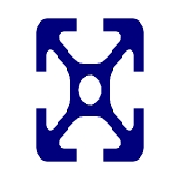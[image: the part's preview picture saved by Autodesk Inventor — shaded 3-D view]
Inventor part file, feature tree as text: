
AUTODESK INVENTOR PART (.ipt)
format: ipt  version: 2020 (Build 240168000, 168)  size: 276,480 bytes
history: native  units: mm
features: other x16, sketch x8, plane x1, split x1
ambient origin geometry x8: Origin, YZ Plane, XZ Plane, XY Plane, X Axis, Y Axis, Z Axis, Center Point
bodies: Body (feature_tree)
feature tree (26):
  other  "Řízená délka"
  other  "Těleso1"
  other  "Start Plane"
  other  "End Plane"
  other  "iFeatureSketch"
  other  "DRAZKA_20:1"
  other  "DRAZKA_20:2"
  other  "DRAZKA_20:3"
  other  "DRAZKA_20:4"
  other  "DIRA_20:1"
  other  "DRAZKA_20:1Axis"
  other  "DRAZKA_20:2Axis"
  other  "DRAZKA_20:3Axis"
  other  "DRAZKA_20:4Axis"
  other  "DIRA_20:1Axis"
  plane  "Work Plane5"
  split  "Split1"
  sketch  "Sketch"  dims[d2=20.0mm d3=20.0mm d4=2.0mm d9=10.0mm d10=300.0mm d11=0.13mm d12=0.0mm d15=0.83mm d16=0.83mm d17=9.8mm d18=3.0mm d19=4.55mm d20=45.0deg d21=5.2mm d22=1.8mm d24=1.0mm d26=0.83mm d27=0.83mm d28=9.8mm d29=3.0mm d30=4.55mm d31=45.0deg d32=5.2mm d33=1.8mm d35=1.0mm d37=0.83mm d38=0.83mm d39=9.8mm d40=3.0mm d41=4.55mm d42=45.0deg d43=5.2mm d44=1.8mm d46=1.0mm d48=0.83mm d49=0.83mm d50=9.8mm d51=3.0mm d52=4.55mm d53=45.0deg d54=5.2mm d55=1.8mm d57=1.0mm d59=4.3mm d60=0.0mm d61=0.0mm d62=0.0mm d63=0.0mm d64=0.0mm d65=0.0mm d66=0.0mm d67=0.0mm d76=90.0deg d14=290.0mm]
  sketch  "Náčrt11"
  other  "Pracovní rovina4"
  sketch  "Náčrt12"
  sketch  "Náčrt6"
  sketch  "Náčrt7"
  sketch  "Náčrt8"
  sketch  "Náčrt9"
  sketch  "Náčrt10"
